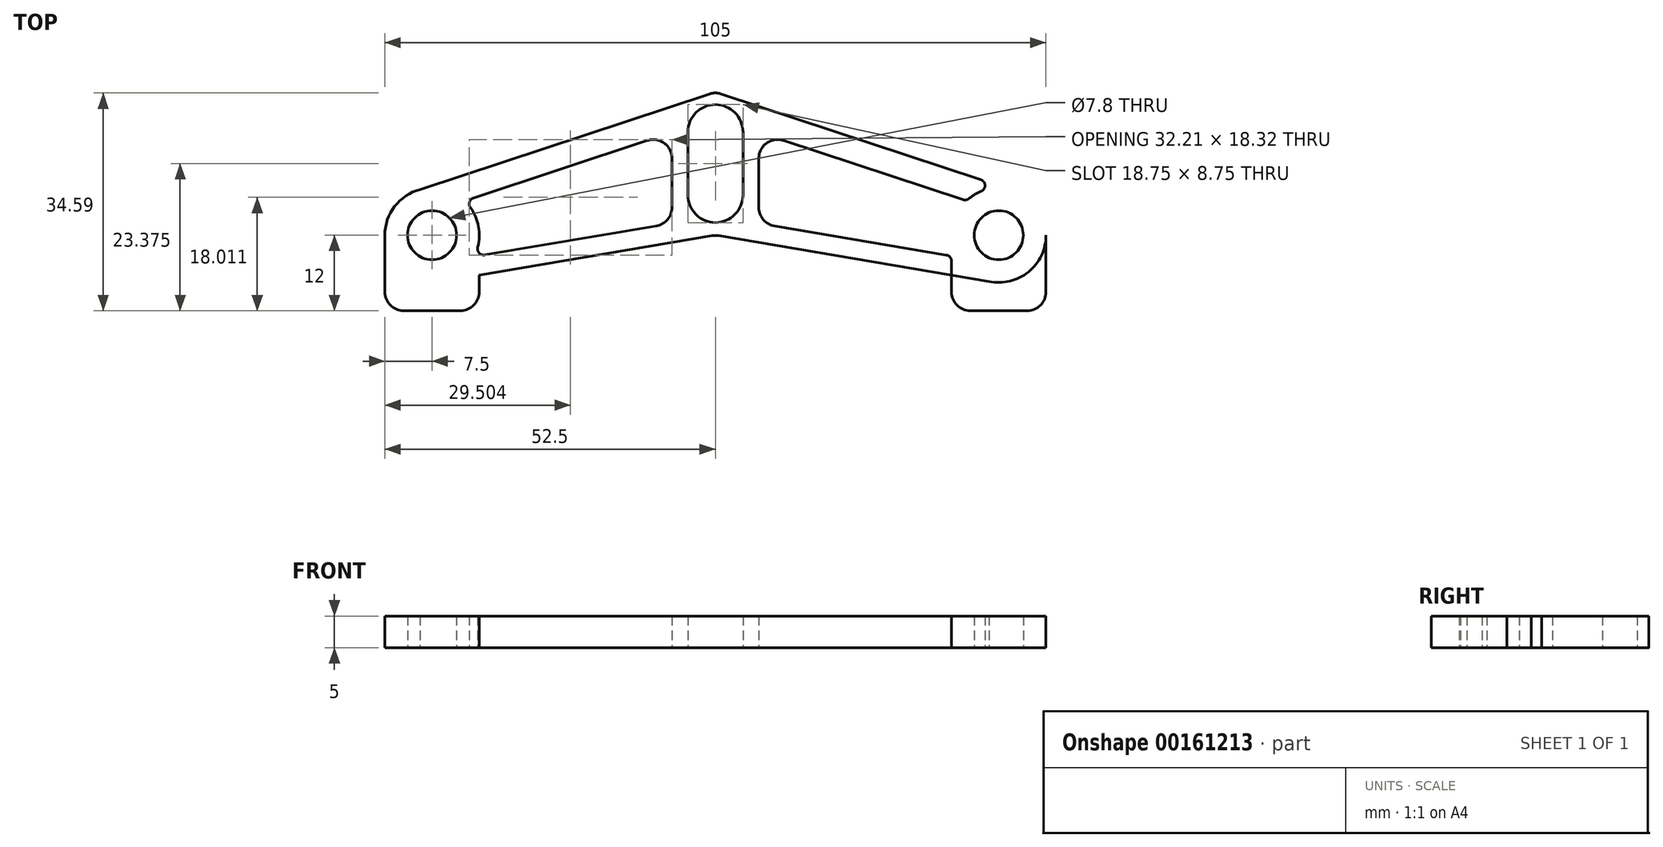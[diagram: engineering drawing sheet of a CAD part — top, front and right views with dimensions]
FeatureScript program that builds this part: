
annotation { "Feature Type Name" : "Feature", "Feature Type Description" : "" }
export const myFeature = defineFeature(function(context is Context, id is Id, definition is map)
    precondition{}
    {
        {
            var Q0;
            Q0=qCreatedBy(makeId("Top.planeOp"),FACE);
            var sketch = newSketch(context, id + "F0", { "sketchPlane" : qUnion([Q0])});
            skCircle(sketch, "E0", {"center": v(-45, 0) * mm, "radius": 7.5 * mm});
            skCircle(sketch, "E1", {"center": v(-45, 0) * mm, "radius": 3.9 * mm});
            skLineSegment(sketch, "E2", {"start": v(-0.94, 22.44) * mm, "end": v(-46.9, 7.25) * mm});
            skPoint(sketch, "E3.middle", {"position": v(0, 17.02) * mm});
            skLineSegment(sketch, "E4", {"start": v(-0.5, -0.08) * mm, "end": v(-43.44, -7.34) * mm});
            skCircle(sketch, "E5.MirrorC", {"center": v(45, 0) * mm, "radius": 7.5 * mm});
            skCircle(sketch, "E6.MirrorC", {"center": v(45, 0) * mm, "radius": 3.9 * mm});
            skLineSegment(sketch, "E7.MirrorCS", {"start": v(0.5, -0.08) * mm, "end": v(43.44, -7.34) * mm});
            skLineSegment(sketch, "E8.MirrorCS", {"start": v(0.94, 22.44) * mm, "end": v(46.9, 7.25) * mm});
            skCircle(sketch, "E9", {"center": v(0, 16.38) * mm, "radius": 2.55 * mm});
            skCircle(sketch, "E10", {"center": v(0, 6.38) * mm, "radius": 2.55 * mm});
            skCircle(sketch, "E11", {"center": v(0, 16.38) * mm, "radius": 4.38 * mm});
            skCircle(sketch, "E12", {"center": v(0, 6.38) * mm, "radius": 4.38 * mm});
            skPoint(sketch, "E13.visualSharp", {"position": v(0, 22.75) * mm});
            skArc(sketch, "E13.filletArc", {"start": v(0.94, 22.44) * mm, "mid": v(0, 22.6) * mm, "end": v(-0.94, 22.44) * mm});
            skPoint(sketch, "E14.visualSharp", {"position": v(0, 0) * mm});
            skArc(sketch, "E14.filletArc", {"start": v(0.5, -0.08) * mm, "mid": v(0, -0.04) * mm, "end": v(-0.5, -0.08) * mm});
            skLineSegment(sketch, "E15.bottom", {"start": v(-10.83, 15.03) * mm, "end": v(-39.84, 5.45) * mm});
            skLineSegment(sketch, "E15.top", {"start": v(-9.4, 1.46) * mm, "end": v(-38.33, -3.43) * mm});
            skLineSegment(sketch, "E15.left", {"start": v(-6.9, 12.18) * mm, "end": v(-6.9, 4.41) * mm});
            skPoint(sketch, "E16.visualSharp", {"position": v(-6.9, 16.33) * mm});
            skArc(sketch, "E16.filletArc", {"start": v(-6.9, 12.18) * mm, "mid": v(-8.13, 14.61) * mm, "end": v(-10.83, 15.03) * mm});
            skPoint(sketch, "E17.visualSharp", {"position": v(-6.9, 1.88) * mm});
            skArc(sketch, "E17.filletArc", {"start": v(-9.4, 1.46) * mm, "mid": v(-7.6, 2.48) * mm, "end": v(-6.9, 4.41) * mm});
            skArc(sketch, "E18.MirrorCS", {"start": v(34.6, -1.45) * mm, "mid": v(34.75, 2.26) * mm, "end": v(36.17, 5.68) * mm});
            skArc(sketch, "E19.MirrorCS", {"start": v(38.98, -2.14) * mm, "mid": v(39.14, -3.03) * mm, "end": v(38.33, -3.43) * mm});
            skLineSegment(sketch, "E20.MirrorCS", {"start": v(9.4, 1.46) * mm, "end": v(38.33, -3.43) * mm});
            skArc(sketch, "E21.MirrorCS", {"start": v(9.4, 1.46) * mm, "mid": v(7.6, 2.48) * mm, "end": v(6.9, 4.41) * mm});
            skLineSegment(sketch, "E22.MirrorCS", {"start": v(6.9, 12.18) * mm, "end": v(6.9, 4.41) * mm});
            skLineSegment(sketch, "E23.MirrorCS", {"start": v(10.83, 15.03) * mm, "end": v(39.84, 5.45) * mm});
            skArc(sketch, "E24.MirrorCS", {"start": v(39.84, 5.45) * mm, "mid": v(40.31, 4.98) * mm, "end": v(40.24, 4.33) * mm});
            skArc(sketch, "E25.MirrorCS", {"start": v(6.9, 12.18) * mm, "mid": v(8.13, 14.61) * mm, "end": v(10.83, 15.03) * mm});
            skLineSegment(sketch, "E26.bottom", {"start": v(37.5, 0) * mm, "end": v(52.5, 0) * mm});
            skLineSegment(sketch, "E26.top", {"start": v(37.5, -12) * mm, "end": v(52.5, -12) * mm});
            skLineSegment(sketch, "E26.left", {"start": v(37.5, 0) * mm, "end": v(37.5, -12) * mm});
            skLineSegment(sketch, "E26.right", {"start": v(52.5, 0) * mm, "end": v(52.5, -12) * mm});
            skLineSegment(sketch, "E27.MirrorCS", {"start": v(-37.5, 0) * mm, "end": v(-37.5, -12) * mm});
            skLineSegment(sketch, "E28.MirrorCS", {"start": v(-52.5, 0) * mm, "end": v(-52.5, -12) * mm});
            skLineSegment(sketch, "E29.MirrorCS", {"start": v(-37.5, -12) * mm, "end": v(-52.5, -12) * mm});
            skLineSegment(sketch, "E30", {"start": v(4.38, 16.38) * mm, "end": v(4.38, 6.38) * mm});
            skLineSegment(sketch, "E31", {"start": v(-4.38, 16.38) * mm, "end": v(-4.38, 6.38) * mm});
            skSolve(sketch);
        }
        {
            var Q0;
            {var subQ4=sQuery(id+"F0.wireOp",EDGE,"E4");Q0=makeQuery(id+"F0.imprint","IMPRINT",FACE,{"disambiguationData":[TD([[makeQuery(id+"F0.imprint","IMPRINT",EDGE,{"derivedFrom":subQ4}),-1.0]])]});}
            var Q1;
            Q1=makeQuery(id+"F0.imprint","IMPRINT",FACE,{"disambiguationData":[TD([[makeQuery(id+"F0.imprint","IMPRINT",EDGE,{"derivedFrom":sQuery(id+"F0.wireOp",EDGE,"E1")}),-1.0]])]});
            var Q2;
            Q2=makeQuery(id+"F0.imprint","IMPRINT",FACE,{"disambiguationData":[TD([[makeQuery(id+"F0.imprint","IMPRINT",EDGE,{"derivedFrom":sQuery(id+"F0.wireOp",EDGE,"E6.MirrorC")}),1.0]])]});
            var Q3;
            {var subQ12=sQuery(id+"F0.wireOp",EDGE,"E2");Q3=makeQuery(id+"F0.imprint","IMPRINT",FACE,{"disambiguationData":[TD([[makeQuery(id+"F0.imprint","IMPRINT",EDGE,{"derivedFrom":subQ12}),1.0]])]});}
            var Q4;
            {var subQ0=sQuery(id+"F0.wireOp",EDGE,"E7.MirrorCS");var subQ1=sQuery(id+"F0.wireOp",EDGE,"E5.MirrorC");var subQ2=makeQuery(id+"F0.imprint","INTERSECT",VERTEX,{"derivedFrom":[subQ1,subQ0]});Q4=makeQuery(id+"F0.imprint","IMPRINT",FACE,{"disambiguationData":[TD([[makeQuery(id+"F0.imprint","IMPRINT",EDGE,{"disambiguationData":[TD([[subQ2,-1.0]])],"derivedFrom":subQ1}),1.0]])]});}
            var Q5;
            {var subQ5=sQuery(id+"F0.wireOp",EDGE,"E26.top");Q5=makeQuery(id+"F0.imprint","IMPRINT",FACE,{"disambiguationData":[TD([[makeQuery(id+"F0.imprint","IMPRINT",EDGE,{"derivedFrom":subQ5}),1.0]])]});}
            var Q6;
            {var subQ0=sQuery(id+"F0.wireOp",EDGE,"E28.MirrorCS");Q6=makeQuery(id+"F0.imprint","IMPRINT",FACE,{"disambiguationData":[TD([[makeQuery(id+"F0.imprint","IMPRINT",EDGE,{"derivedFrom":subQ0}),1.0]])]});}
            extrude(context, id + "F1", {"entities" : qUnion([Q0, Q1, Q2, Q3, Q4, Q5, Q6]), "depth" : 5 * mm});
        }
        {
            var Q0;
            Q0=makeQuery(id+"F0.imprint","IMPRINT",FACE,{"disambiguationData":[TD([[makeQuery(id+"F0.imprint","IMPRINT",EDGE,{"derivedFrom":sQuery(id+"F0.wireOp",EDGE,"E1")}),1.0]])]});
            var Q1;
            Q1=makeQuery(id+"F0.imprint","IMPRINT",FACE,{"disambiguationData":[TD([[makeQuery(id+"F0.imprint","IMPRINT",EDGE,{"derivedFrom":sQuery(id+"F0.wireOp",EDGE,"E6.MirrorC")}),-1.0]])]});
            extrude(context, id + "F2", {"entities" : qUnion([Q0, Q1]), "operationType" : NewBodyOperationType.REMOVE, "depth" : 25 * mm});
        }
        {
            var Q0;
            Q0=makeQuery(id+"F1.opExtrude","SWEPT_EDGE",EDGE,{"disambiguationData":[OSD([sQuery(id+"F0.wireOp",EDGE,"E0"),sQuery(id+"F0.wireOp",EDGE,"E15.bottom")])]});
            var Q1;
            Q1=makeQuery(id+"F1.opExtrude","SWEPT_EDGE",EDGE,{"disambiguationData":[OSD([sQuery(id+"F0.wireOp",EDGE,"E0"),sQuery(id+"F0.wireOp",EDGE,"E15.top")])]});
            var Q2;
            Q2=makeQuery(id+"F1.opExtrude","SWEPT_EDGE",EDGE,{"disambiguationData":[OSD([sQuery(id+"F0.wireOp",EDGE,"E5.MirrorC"),sQuery(id+"F0.wireOp",EDGE,"E23.MirrorCS")])]});
            var Q3;
            Q3=makeQuery(id+"F1.opExtrude","SWEPT_EDGE",EDGE,{"disambiguationData":[OSD([sQuery(id+"F0.wireOp",EDGE,"E5.MirrorC"),sQuery(id+"F0.wireOp",EDGE,"E20.MirrorCS")])]});
            fillet(context, id + "F3", {"entities" : qUnion([Q0, Q1, Q2, Q3]), "radius" : 1 * mm, "tangentPropagation" : true, "allowEdgeOverflow" : false});
        }
        {
            var Q0;
            Q0=makeQuery(id+"F1.opExtrude","SWEPT_EDGE",EDGE,{"disambiguationData":[OSD([sQuery(id+"F0.wireOp",EDGE,"E28.MirrorCS"),sQuery(id+"F0.wireOp",EDGE,"E29.MirrorCS")])]});
            var Q1;
            Q1=makeQuery(id+"F1.opExtrude","SWEPT_EDGE",EDGE,{"disambiguationData":[OSD([sQuery(id+"F0.wireOp",EDGE,"E27.MirrorCS"),sQuery(id+"F0.wireOp",EDGE,"E29.MirrorCS")])]});
            var Q2;
            Q2=makeQuery(id+"F1.opExtrude","SWEPT_EDGE",EDGE,{"disambiguationData":[OSD([sQuery(id+"F0.wireOp",EDGE,"E26.top"),sQuery(id+"F0.wireOp",EDGE,"E26.left")])]});
            var Q3;
            Q3=makeQuery(id+"F1.opExtrude","SWEPT_EDGE",EDGE,{"disambiguationData":[OSD([sQuery(id+"F0.wireOp",EDGE,"E26.top"),sQuery(id+"F0.wireOp",EDGE,"E26.right")])]});
            fillet(context, id + "F4", {"entities" : qUnion([Q0, Q1, Q2, Q3]), "radius" : 3 * mm, "tangentPropagation" : true, "allowEdgeOverflow" : false});
        }
    });
